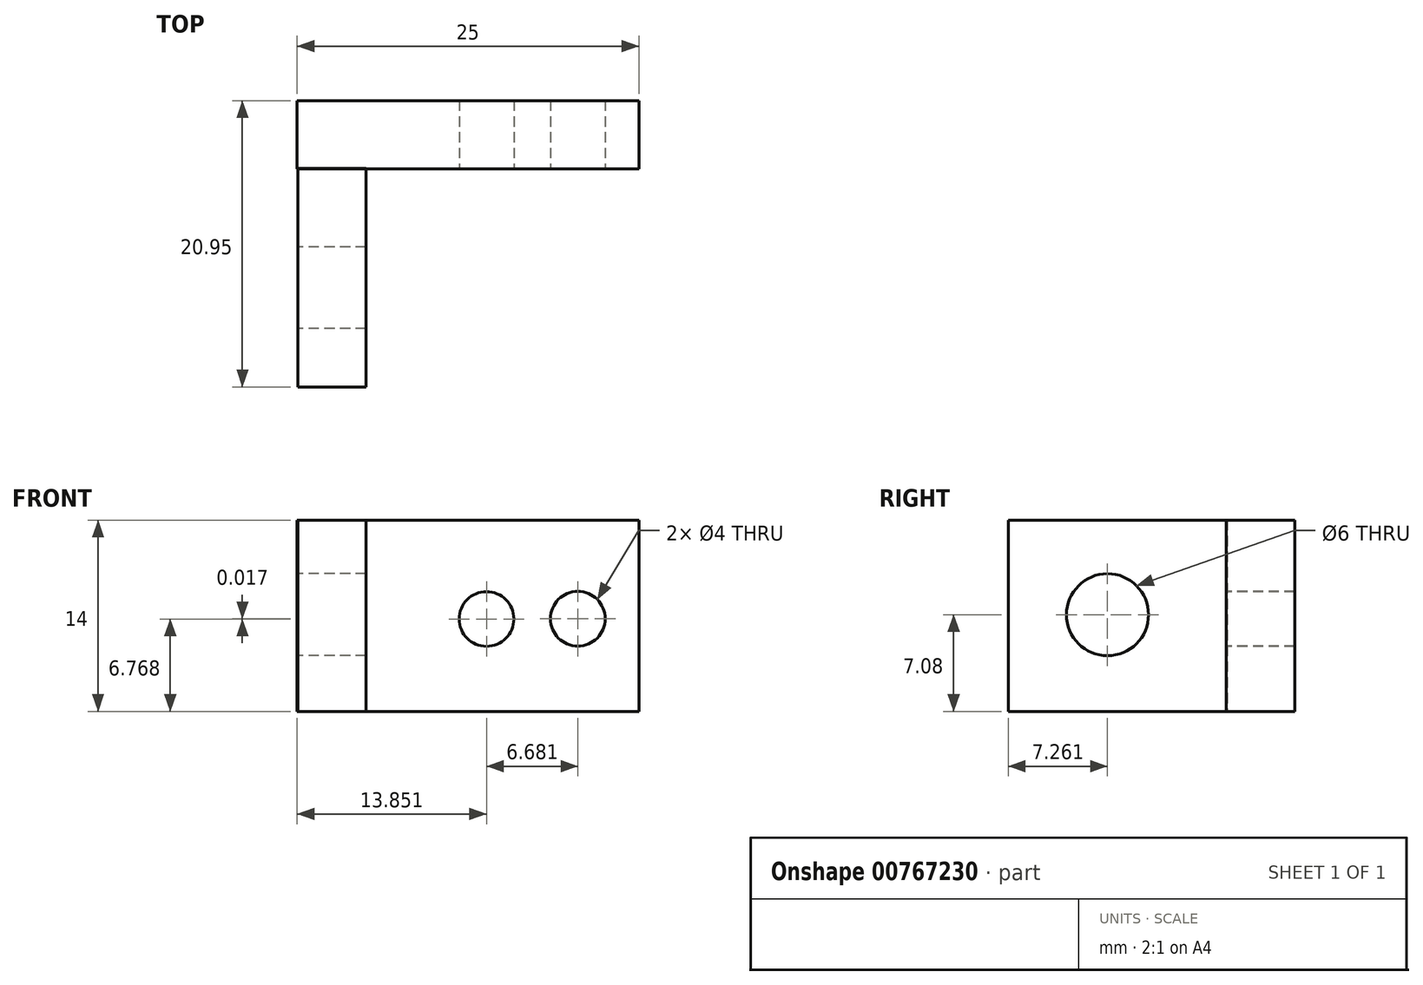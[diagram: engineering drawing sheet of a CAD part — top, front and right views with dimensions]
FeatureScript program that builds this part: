
annotation { "Feature Type Name" : "Feature", "Feature Type Description" : "" }
export const myFeature = defineFeature(function(context is Context, id is Id, definition is map)
    precondition{}
    {
        {
            var Q0;
            Q0=qCreatedBy(makeId("Top.planeOp"),FACE);
            var sketch = newSketch(context, id + "F0", { "sketchPlane" : qUnion([Q0])});
            skLineSegment(sketch, "E0.bottom", {"start": v(0, 15.96) * mm, "end": v(5, 15.96) * mm});
            skLineSegment(sketch, "E0.top", {"start": v(0, -0.04) * mm, "end": v(5, -0.04) * mm});
            skLineSegment(sketch, "E0.left", {"start": v(0, 15.96) * mm, "end": v(0, -0.04) * mm});
            skLineSegment(sketch, "E0.right", {"start": v(5, 15.96) * mm, "end": v(5, -0.04) * mm});
            skLineSegment(sketch, "E1.bottom", {"start": v(-0.04, 15.9) * mm, "end": v(24.96, 15.9) * mm});
            skLineSegment(sketch, "E1.top", {"start": v(-0.04, 20.9) * mm, "end": v(24.96, 20.9) * mm});
            skLineSegment(sketch, "E1.left", {"start": v(-0.04, 15.9) * mm, "end": v(-0.04, 20.9) * mm});
            skLineSegment(sketch, "E1.right", {"start": v(24.96, 15.9) * mm, "end": v(24.96, 20.9) * mm});
            skSolve(sketch);
        }
        {
            var Q0;
            {var subQ5=sQuery(id+"F0.wireOp",EDGE,"E0.bottom");Q0=makeQuery(id+"F0.imprint","IMPRINT",FACE,{"disambiguationData":[TD([[makeQuery(id+"F0.imprint","IMPRINT",EDGE,{"derivedFrom":subQ5}),1.0]])]});}
            var Q1;
            {var subQ0=sQuery(id+"F0.wireOp",EDGE,"E0.top");Q1=makeQuery(id+"F0.imprint","IMPRINT",FACE,{"disambiguationData":[TD([[makeQuery(id+"F0.imprint","IMPRINT",EDGE,{"derivedFrom":subQ0}),1.0]])]});}
            extrude(context, id + "F1", {"entities" : qUnion([Q0, Q1]), "depth" : 14 * mm, "offsetDistance" : 25 * mm});
        }
        {
            var Q0;
            Q0=qCreatedBy(makeId("Right.planeOp"),FACE);
            var sketch = newSketch(context, id + "F2", { "sketchPlane" : qUnion([Q0])});
            skCircle(sketch, "E2", {"center": v(7.22, 7.08) * mm, "radius": 3 * mm});
            skSolve(sketch);
        }
        {
            var Q0;
            Q0=makeQuery(id+"F2.imprint","IMPRINT",FACE,{"disambiguationData":[TD([[makeQuery(id+"F2.imprint","IMPRINT",EDGE,{"derivedFrom":sQuery(id+"F2.wireOp",EDGE,"E2")}),1.0]])]});
            extrude(context, id + "F3", {"entities" : qUnion([Q0]), "operationType" : NewBodyOperationType.REMOVE, "depth" : 9.3 * mm, "offsetDistance" : 25 * mm});
        }
        {
            var Q0;
            Q0=qCreatedBy(makeId("Front.planeOp"),FACE);
            var sketch = newSketch(context, id + "F4", { "sketchPlane" : qUnion([Q0])});
            skCircle(sketch, "E3", {"center": v(20.5, 6.78) * mm, "radius": 2 * mm});
            skCircle(sketch, "E4", {"center": v(13.81, 6.77) * mm, "radius": 2 * mm});
            skSolve(sketch);
        }
        {
            var Q0;
            Q0=makeQuery(id+"F4.imprint","IMPRINT",FACE,{"disambiguationData":[TD([[makeQuery(id+"F4.imprint","IMPRINT",EDGE,{"derivedFrom":sQuery(id+"F4.wireOp",EDGE,"E4")}),1.0]])]});
            var Q1;
            Q1=makeQuery(id+"F4.imprint","IMPRINT",FACE,{"disambiguationData":[TD([[makeQuery(id+"F4.imprint","IMPRINT",EDGE,{"derivedFrom":sQuery(id+"F4.wireOp",EDGE,"E3")}),1.0]])]});
            extrude(context, id + "F5", {"entities" : qUnion([Q0, Q1]), "operationType" : NewBodyOperationType.REMOVE, "oppositeDirection" : true, "depth" : 25 * mm, "offsetDistance" : 25 * mm});
        }
    });
